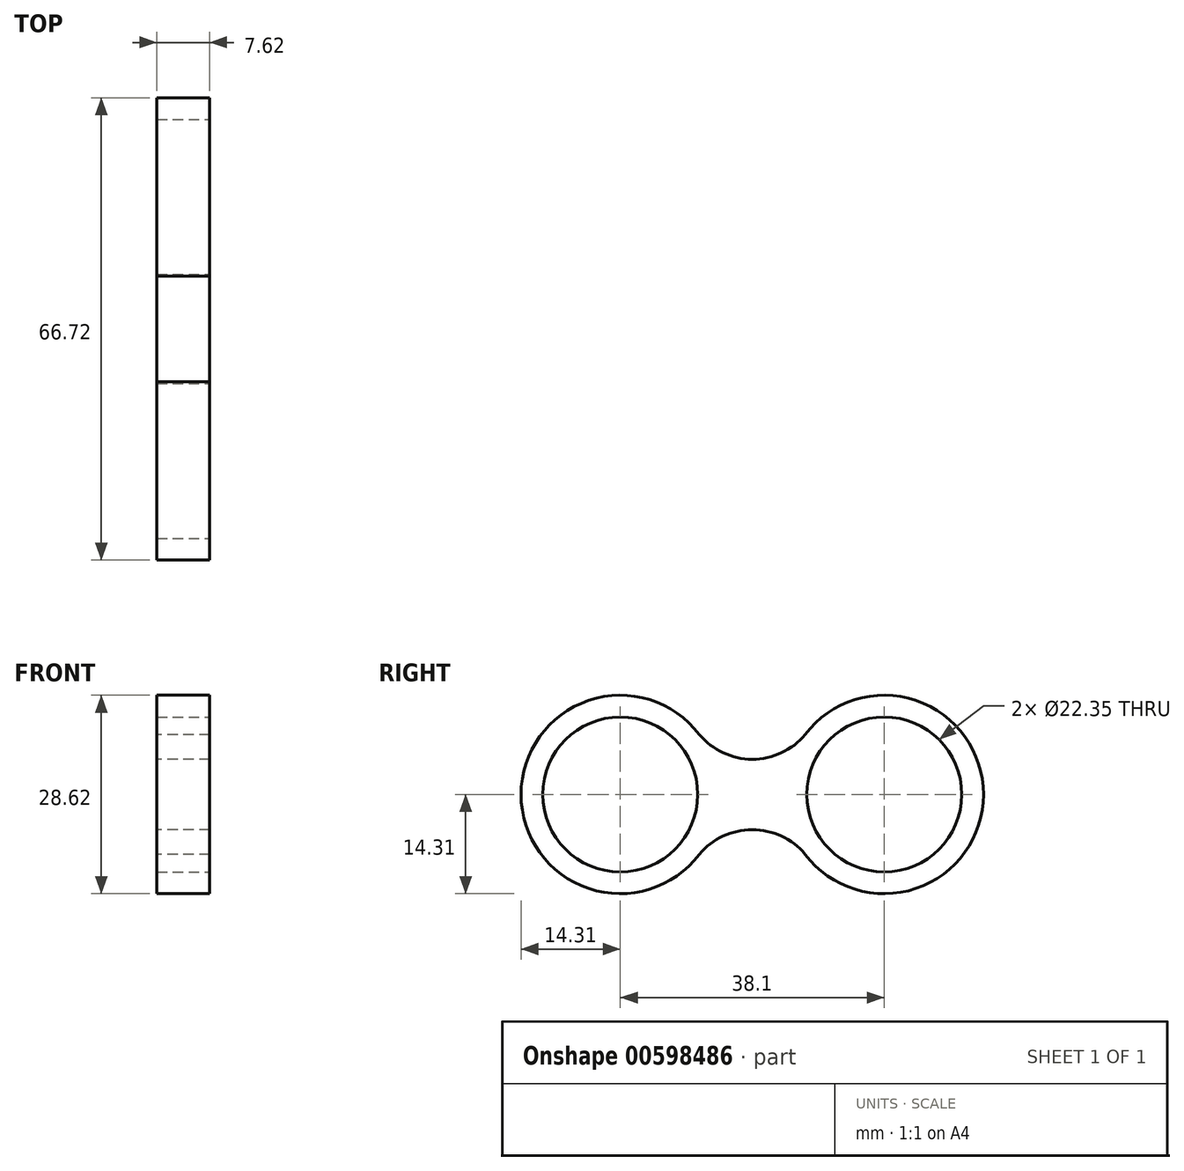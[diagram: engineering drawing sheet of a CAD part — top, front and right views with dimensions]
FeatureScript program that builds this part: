
annotation { "Feature Type Name" : "Feature", "Feature Type Description" : "" }
export const myFeature = defineFeature(function(context is Context, id is Id, definition is map)
    precondition{}
    {
        {
            var Q0;
            Q0=qCreatedBy(makeId("Right.planeOp"),FACE);
            var sketch = newSketch(context, id + "F0", { "sketchPlane" : qUnion([Q0])});
            skPoint(sketch, "E0", {"position": v(-19.05, 0) * mm});
            skPoint(sketch, "E1", {"position": v(19.05, 0) * mm});
            skArc(sketch, "E2", {"start": v(-7.64, 8.64) * mm, "mid": v(-33.36, 0) * mm, "end": v(-7.64, -8.64) * mm});
            skCircle(sketch, "E3", {"center": v(-19.05, 0) * mm, "radius": 11.14 * mm});
            skArc(sketch, "E4", {"start": v(7.64, -8.64) * mm, "mid": v(33.36, 0) * mm, "end": v(7.64, 8.64) * mm});
            skCircle(sketch, "E5", {"center": v(19.05, 0) * mm, "radius": 11.14 * mm});
            skArc(sketch, "E6", {"start": v(-7.64, 8.64) * mm, "mid": v(0, 5.08) * mm, "end": v(7.64, 8.64) * mm});
            skArc(sketch, "E7", {"start": v(7.64, -8.64) * mm, "mid": v(0, -5.08) * mm, "end": v(-7.64, -8.64) * mm});
            skSolve(sketch);
        }
        {
            var Q0;
            Q0=makeQuery(id+"F0.imprint","IMPRINT",FACE,{"disambiguationData":[TD([[makeQuery(id+"F0.imprint","IMPRINT",EDGE,{"derivedFrom":sQuery(id+"F0.wireOp",EDGE,"E2")}),1.0]])]});
            extrude(context, id + "F1", {"entities" : qUnion([Q0]), "depth" : 7.62 * mm, "offsetDistance" : 25.4 * mm});
        }
        {
            var Q0;
            Q0=sQuery(id+"F0.wireOp",VERTEX,"E1");
            var Q1;
            Q1=sQuery(id+"F0.wireOp",VERTEX,"E0");
            var Q2;
            Q2=makeQuery(id+"F1.opExtrude","SWEPT_BODY",BODY,{"disambiguationData":[OSD([sQuery(id+"F0.wireOp",EDGE,"E2"),sQuery(id+"F0.wireOp",EDGE,"E3"),sQuery(id+"F0.wireOp",EDGE,"E4"),sQuery(id+"F0.wireOp",EDGE,"E5"),sQuery(id+"F0.wireOp",EDGE,"E6"),sQuery(id+"F0.wireOp",EDGE,"E7")])]});
            hole(context, id + "F2", {"style" : HoleStyle.SIMPLE, "endStyle" : HoleEndStyle.THROUGH, "oppositeDirection" : true, "holeDiameter" : 22.35 * mm, "majorDiameter" : 6.35 * mm, "isTappedThrough" : true, "tappedDepth" : 15.24 * mm, "tapClearance" : 3, "locations" : qUnion([Q0, Q1]), "scope" : qUnion([Q2]), "startStyle" : HoleStartStyle.SKETCH});
        }
    });
